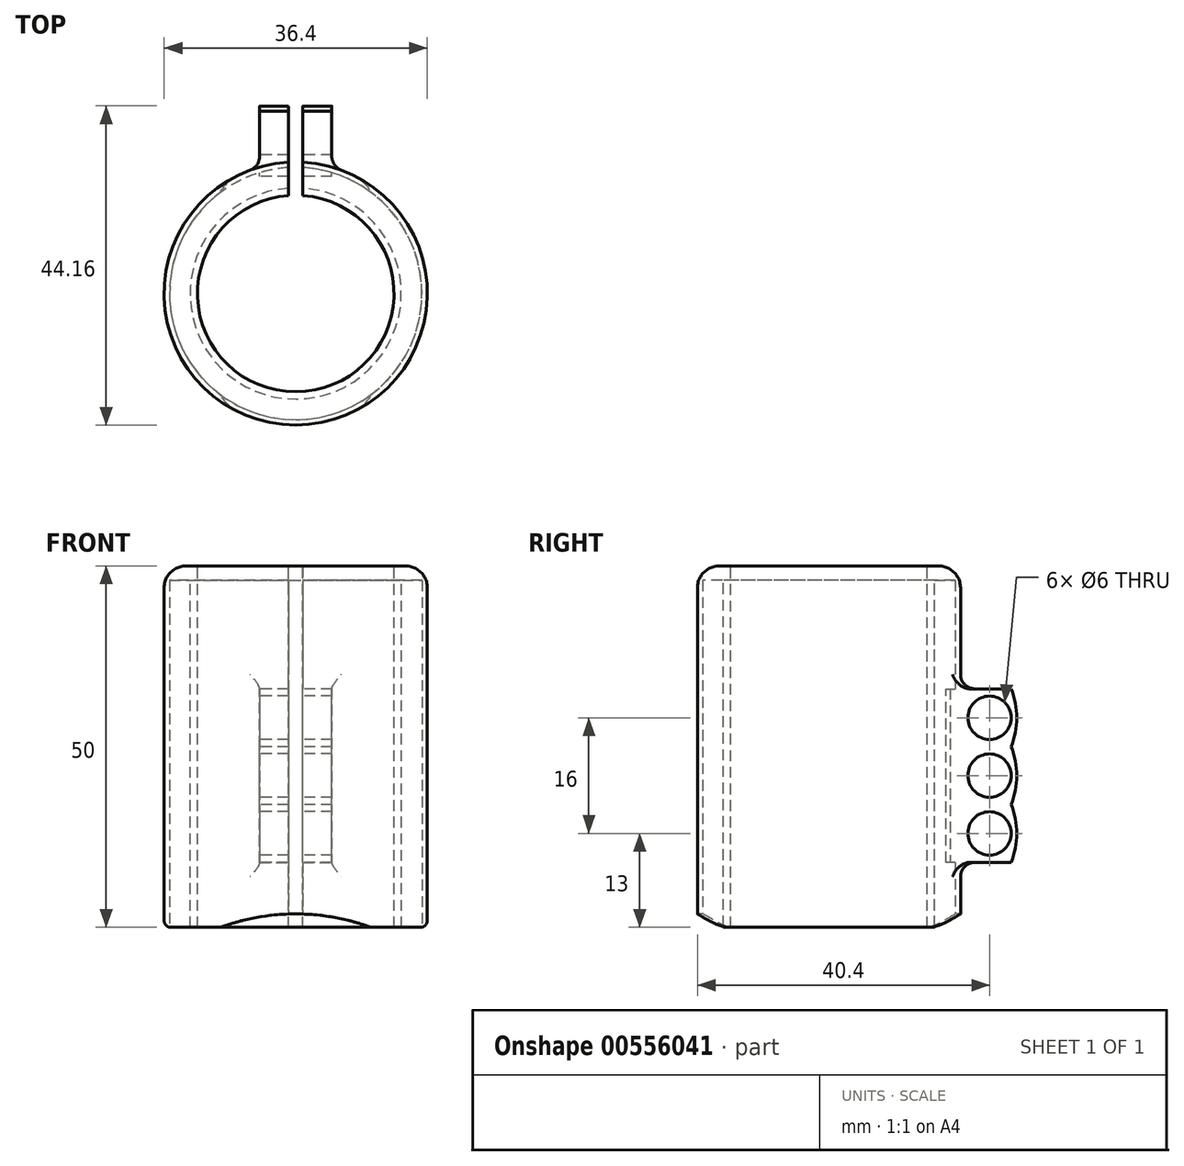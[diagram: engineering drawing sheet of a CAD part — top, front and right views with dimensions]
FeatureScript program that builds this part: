
annotation { "Feature Type Name" : "Feature", "Feature Type Description" : "" }
export const myFeature = defineFeature(function(context is Context, id is Id, definition is map)
    precondition{}
    {
        {
            var Q0;
            Q0=qCreatedBy(makeId("Top.planeOp"),FACE);
            var sketch = newSketch(context, id + "F0", { "sketchPlane" : qUnion([Q0])});
            skCircle(sketch, "E0", {"center": v(0, 0) * mm, "radius": 17.45 * mm});
            skCircle(sketch, "E1", {"center": v(0, 0) * mm, "radius": 18.2 * mm});
            skSolve(sketch);
        }
        {
            var Q0;
            Q0=makeQuery(id+"F0.imprint","IMPRINT",FACE,{"disambiguationData":[TD([[makeQuery(id+"F0.imprint","IMPRINT",EDGE,{"derivedFrom":sQuery(id+"F0.wireOp",EDGE,"E0")}),-1.0]])]});
            extrude(context, id + "F1", {"entities" : qUnion([Q0]), "depth" : 50 * mm, "offsetDistance" : 25 * mm});
        }
        {
            var Q0;
            Q0=qCreatedBy(makeId("Front.planeOp"),FACE);
            var sketch = newSketch(context, id + "F2", { "sketchPlane" : qUnion([Q0])});
            skLineSegment(sketch, "E2", {"start": v(-10.4, 0) * mm, "end": v(10.4, 0) * mm});
            skArc(sketch, "E3", {"start": v(10.4, 0) * mm, "mid": v(0, 1.86) * mm, "end": v(-10.4, 0) * mm});
            skPoint(sketch, "E4", {"position": v(0, 25) * mm});
            skLineSegment(sketch, "E5", {"start": v(46.29, 25) * mm, "end": v(-63.22, 25) * mm, "construction": true});
            skSolve(sketch);
        }
        {
            var Q0;
            Q0 = qSketchRegion(id + "F2", true);
            var Q1;
            Q1=sQuery(id+"F2.wireOp",EDGE,"E2");
            var Q2;
            Q2=sQuery(id+"F2.wireOp",EDGE,"E3");
            extrude(context, id + "F3", {"entities" : qUnion([Q0]), "operationType" : NewBodyOperationType.REMOVE, "surfaceEntities" : qUnion([Q1, Q2]), "endBound" : BoundingType.SYMMETRIC, "oppositeDirection" : true, "depth" : 190 * mm, "offsetDistance" : 25 * mm});
        }
        {
            var Q0;
            Q0=makeQuery(id+"F1.opExtrude","CAP_FACE",FACE,{"disambiguationData":[OSD([sQuery(id+"F0.wireOp",EDGE,"E0"),sQuery(id+"F0.wireOp",EDGE,"E1")])],"isStart":false});
            var sketch = newSketch(context, id + "F4", { "sketchPlane" : qUnion([Q0])});
            skCircle(sketch, "E6", {"center": v(0, 0) * mm, "radius": 14.6 * mm});
            skCircle(sketch, "E7", {"center": v(0, 0) * mm, "radius": 13.6 * mm});
            skSolve(sketch);
        }
        {
            var Q0;
            Q0=makeQuery(id+"F4.imprint","IMPRINT",FACE,{"disambiguationData":[TD([[makeQuery(id+"F4.imprint","IMPRINT",EDGE,{"derivedFrom":sQuery(id+"F4.wireOp",EDGE,"E6")}),1.0]])]});
            extrude(context, id + "F5", {"entities" : qUnion([Q0]), "oppositeDirection" : true, "depth" : 50 * mm, "offsetDistance" : 25 * mm});
        }
        {
            var Q0;
            Q0=makeQuery(id+"F5.opExtrude","CAP_FACE",FACE,{"disambiguationData":[OSD([sQuery(id+"F4.wireOp",EDGE,"E6"),sQuery(id+"F4.wireOp",EDGE,"E7")])],"isStart":true});
            var sketch = newSketch(context, id + "F6", { "sketchPlane" : qUnion([Q0])});
            skCircle(sketch, "E8", {"center": v(0, 0) * mm, "radius": 17.45 * mm});
            skCircle(sketch, "E9", {"center": v(0, 0) * mm, "radius": 14.6 * mm});
            skSolve(sketch);
        }
        {
            var Q0;
            Q0=makeQuery(id+"F6.imprint","IMPRINT",FACE,{"disambiguationData":[TD([[makeQuery(id+"F6.imprint","IMPRINT",EDGE,{"derivedFrom":sQuery(id+"F6.wireOp",EDGE,"E8")}),1.0]])]});
            extrude(context, id + "F7", {"entities" : qUnion([Q0]), "operationType" : NewBodyOperationType.ADD, "oppositeDirection" : true, "depth" : 2 * mm, "offsetDistance" : 25 * mm});
        }
        {
            var Q0;
            Q0=qCreatedBy(makeId("Right.planeOp"),FACE);
            var sketch = newSketch(context, id + "F8", { "sketchPlane" : qUnion([Q0])});
            skPoint(sketch, "E10", {"position": v(18.2, 0) * mm});
            skPoint(sketch, "E11", {"position": v(18.2, 25) * mm});
            skLineSegment(sketch, "E12.MirrorCS", {"start": v(17.2, 33) * mm, "end": v(25.2, 33) * mm});
            skPoint(sketch, "E13", {"position": v(22.2, 21) * mm});
            skCircle(sketch, "E14", {"center": v(22.2, 21) * mm, "radius": 3 * mm});
            skCircle(sketch, "E15.MirrorC", {"center": v(22.2, 29) * mm, "radius": 3 * mm});
            skLineSegment(sketch, "E16.MirrorCS", {"start": v(25.2, 33) * mm, "end": v(16.2, 33) * mm});
            skLineSegment(sketch, "E17", {"start": v(16.2, 17) * mm, "end": v(16.2, 33) * mm});
            skPoint(sketch, "E18", {"position": v(25.2, 25) * mm});
            skArc(sketch, "E19", {"start": v(25.2, 17) * mm, "mid": v(25.96, 21) * mm, "end": v(25.2, 25) * mm});
            skArc(sketch, "E20", {"start": v(25.2, 25) * mm, "mid": v(25.96, 29) * mm, "end": v(25.2, 33) * mm});
            skArc(sketch, "E21.MirrorCS", {"start": v(25.2, 17) * mm, "mid": v(25.96, 13) * mm, "end": v(25.2, 9) * mm});
            skCircle(sketch, "E22.MirrorC", {"center": v(22.2, 13) * mm, "radius": 3 * mm});
            skLineSegment(sketch, "E23", {"start": v(25.2, 9) * mm, "end": v(16.2, 9) * mm});
            skLineSegment(sketch, "E24", {"start": v(16.2, 9) * mm, "end": v(16.2, 17) * mm});
            skSolve(sketch);
        }
        {
            var Q0;
            Q0 = qSketchRegion(id + "F8", true);
            extrude(context, id + "F9", {"entities" : qUnion([Q0]), "operationType" : NewBodyOperationType.ADD, "endBound" : BoundingType.SYMMETRIC, "depth" : 10 * mm, "offsetDistance" : 25 * mm});
        }
        {
            var Q0;
            Q0=qCreatedBy(makeId("Front.planeOp"),FACE);
            var sketch = newSketch(context, id + "F10", { "sketchPlane" : qUnion([Q0])});
            skLineSegment(sketch, "E25", {"start": v(0, 0) * mm, "end": v(0, 53.47) * mm, "construction": true});
            skPoint(sketch, "E26", {"position": v(0, 25) * mm});
            skLineSegment(sketch, "E27", {"start": v(0.25, 0) * mm, "end": v(-0.25, 0) * mm});
            skLineSegment(sketch, "E28", {"start": v(1, 25) * mm, "end": v(-1, 25) * mm});
            skLineSegment(sketch, "E29", {"start": v(1, 0) * mm, "end": v(1, 53.47) * mm});
            skLineSegment(sketch, "E30", {"start": v(1, 53.47) * mm, "end": v(-1, 53.47) * mm});
            skLineSegment(sketch, "E31", {"start": v(-1, 53.47) * mm, "end": v(-1, 0) * mm});
            skLineSegment(sketch, "E32", {"start": v(-1, 0) * mm, "end": v(1, 0) * mm});
            skSolve(sketch);
        }
        {
            var Q0;
            Q0 = qSketchRegion(id + "F10", true);
            extrude(context, id + "F11", {"entities" : qUnion([Q0]), "operationType" : NewBodyOperationType.REMOVE, "oppositeDirection" : true, "depth" : 39.9 * mm, "offsetDistance" : 25 * mm});
        }
        {
            var Q0;
            Q0=makeQuery(id+"F1.opExtrude","CAP_EDGE",EDGE,{"disambiguationData":[OSD([sQuery(id+"F0.wireOp",EDGE,"E1")])],"isStart":false});
            fillet(context, id + "F12", {"entities" : qUnion([Q0]), "radius" : 3 * mm, "tangentPropagation" : true, "allowEdgeOverflow" : false});
        }
        {
            var Q0;
            Q0=makeQuery(id+"F9.boolean.opBoolean","INTERSECT",EDGE,{"derivedFrom":[makeQuery(id+"F1.opExtrude","SWEPT_FACE",FACE,{"disambiguationData":[OSD([sQuery(id+"F0.wireOp",EDGE,"E1")])]}),makeQuery(id+"F9.opExtrude","CAP_FACE",FACE,{"disambiguationData":[OSD([sQuery(id+"F8.wireOp",EDGE,"VbptmBmL-QUm1-pIPm-j6ny-vpmM6alW8hsR"),sQuery(id+"F8.wireOp",EDGE,"2ef763fb-3408-4ae8-8002-a0a4f16cbd950.MirrorCS"),sQuery(id+"F8.wireOp",EDGE,"E14"),sQuery(id+"F8.wireOp",EDGE,"E15.MirrorC"),sQuery(id+"F8.wireOp",EDGE,"N6T6yWEC-n2oh-UMyS-kolp-r8fxWRvXxSvT"),sQuery(id+"F8.wireOp",EDGE,"E16.MirrorCS"),sQuery(id+"F8.wireOp",EDGE,"E17")])],"isStart":true})]});
            var Q1;
            Q1=makeQuery(id+"F9.boolean.opBoolean","INTERSECT",EDGE,{"derivedFrom":[makeQuery(id+"F1.opExtrude","SWEPT_FACE",FACE,{"disambiguationData":[OSD([sQuery(id+"F0.wireOp",EDGE,"E1")])]}),makeQuery(id+"F9.opExtrude","CAP_FACE",FACE,{"disambiguationData":[OSD([sQuery(id+"F8.wireOp",EDGE,"VbptmBmL-QUm1-pIPm-j6ny-vpmM6alW8hsR"),sQuery(id+"F8.wireOp",EDGE,"2ef763fb-3408-4ae8-8002-a0a4f16cbd950.MirrorCS"),sQuery(id+"F8.wireOp",EDGE,"E14"),sQuery(id+"F8.wireOp",EDGE,"E15.MirrorC"),sQuery(id+"F8.wireOp",EDGE,"N6T6yWEC-n2oh-UMyS-kolp-r8fxWRvXxSvT"),sQuery(id+"F8.wireOp",EDGE,"E16.MirrorCS"),sQuery(id+"F8.wireOp",EDGE,"E17")])],"isStart":false})]});
            fillet(context, id + "F13", {"entities" : qUnion([Q0, Q1]), "radius" : 2 * mm, "tangentPropagation" : true, "allowEdgeOverflow" : false});
        }
        {
            var Q0;
            {var subQ0=makeQuery(id+"F1.opExtrude","SWEPT_FACE",FACE,{"disambiguationData":[OSD([sQuery(id+"F0.wireOp",EDGE,"E1")])]});var subQ1=sQuery(id+"F8.wireOp",EDGE,"E16.MirrorCS");var subQ2=makeQuery(id+"F9.opExtrude","SWEPT_FACE",FACE,{"disambiguationData":[OSD([subQ1])]});Q0=makeQuery(id+"F11.boolean.opBoolean","SPLIT",EDGE,{"disambiguationData":[TD([makeQuery(id+"F11.opExtrude","SWEPT_FACE",FACE,{"disambiguationData":[OSD([sQuery(id+"F10.wireOp",EDGE,"E31")])]})])],"derivedFrom":makeQuery(id+"F9.boolean.opBoolean","INTERSECT",EDGE,{"derivedFrom":[subQ0,subQ2]})});}
            var Q1;
            {var subQ0=makeQuery(id+"F1.opExtrude","SWEPT_FACE",FACE,{"disambiguationData":[OSD([sQuery(id+"F0.wireOp",EDGE,"E1")])]});var subQ1=sQuery(id+"F8.wireOp",EDGE,"E16.MirrorCS");var subQ2=makeQuery(id+"F9.opExtrude","SWEPT_FACE",FACE,{"disambiguationData":[OSD([subQ1])]});Q1=makeQuery(id+"F11.boolean.opBoolean","SPLIT",EDGE,{"disambiguationData":[TD([makeQuery(id+"F11.opExtrude","SWEPT_FACE",FACE,{"disambiguationData":[OSD([sQuery(id+"F10.wireOp",EDGE,"E29")])]})])],"derivedFrom":makeQuery(id+"F9.boolean.opBoolean","INTERSECT",EDGE,{"derivedFrom":[subQ0,subQ2]})});}
            fillet(context, id + "F14", {"entities" : qUnion([Q0, Q1]), "radius" : 2 * mm, "tangentPropagation" : true, "allowEdgeOverflow" : false});
        }
        {
            var Q0;
            Q0=makeQuery(id+"F3.boolean.opBoolean","SPLIT",EDGE,{"disambiguationData":[OD(1.0)],"derivedFrom":makeQuery(id+"F1.opExtrude","CAP_EDGE",EDGE,{"disambiguationData":[OSD([sQuery(id+"F0.wireOp",EDGE,"E1")])],"isStart":true})});
            var Q1;
            Q1=makeQuery(id+"F3.boolean.opBoolean","SPLIT",EDGE,{"disambiguationData":[OD(0.0)],"derivedFrom":makeQuery(id+"F1.opExtrude","CAP_EDGE",EDGE,{"disambiguationData":[OSD([sQuery(id+"F0.wireOp",EDGE,"E1")])],"isStart":true})});
            fillet(context, id + "F15", {"entities" : qUnion([Q0, Q1]), "radius" : 1 * mm, "tangentPropagation" : true, "allowEdgeOverflow" : false});
        }
        {
            var Q0;
            {var subQ0=makeQuery(id+"F1.opExtrude","SWEPT_FACE",FACE,{"disambiguationData":[OSD([sQuery(id+"F0.wireOp",EDGE,"E1")])]});var subQ1=sQuery(id+"F8.wireOp",EDGE,"E23");var subQ2=makeQuery(id+"F9.opExtrude","SWEPT_FACE",FACE,{"disambiguationData":[OSD([subQ1])]});Q0=makeQuery(id+"F11.boolean.opBoolean","SPLIT",EDGE,{"disambiguationData":[TD([makeQuery(id+"F11.opExtrude","SWEPT_FACE",FACE,{"disambiguationData":[OSD([sQuery(id+"F10.wireOp",EDGE,"E29")])]})])],"derivedFrom":makeQuery(id+"F9.boolean.opBoolean","INTERSECT",EDGE,{"derivedFrom":[subQ0,subQ2]})});}
            var Q1;
            {var subQ0=makeQuery(id+"F1.opExtrude","SWEPT_FACE",FACE,{"disambiguationData":[OSD([sQuery(id+"F0.wireOp",EDGE,"E1")])]});var subQ1=sQuery(id+"F8.wireOp",EDGE,"E23");var subQ2=makeQuery(id+"F9.opExtrude","SWEPT_FACE",FACE,{"disambiguationData":[OSD([subQ1])]});Q1=makeQuery(id+"F11.boolean.opBoolean","SPLIT",EDGE,{"disambiguationData":[TD([makeQuery(id+"F11.opExtrude","SWEPT_FACE",FACE,{"disambiguationData":[OSD([sQuery(id+"F10.wireOp",EDGE,"E31")])]})])],"derivedFrom":makeQuery(id+"F9.boolean.opBoolean","INTERSECT",EDGE,{"derivedFrom":[subQ0,subQ2]})});}
            fillet(context, id + "F16", {"entities" : qUnion([Q0, Q1]), "radius" : 2 * mm, "tangentPropagation" : true, "allowEdgeOverflow" : false});
        }
    });
